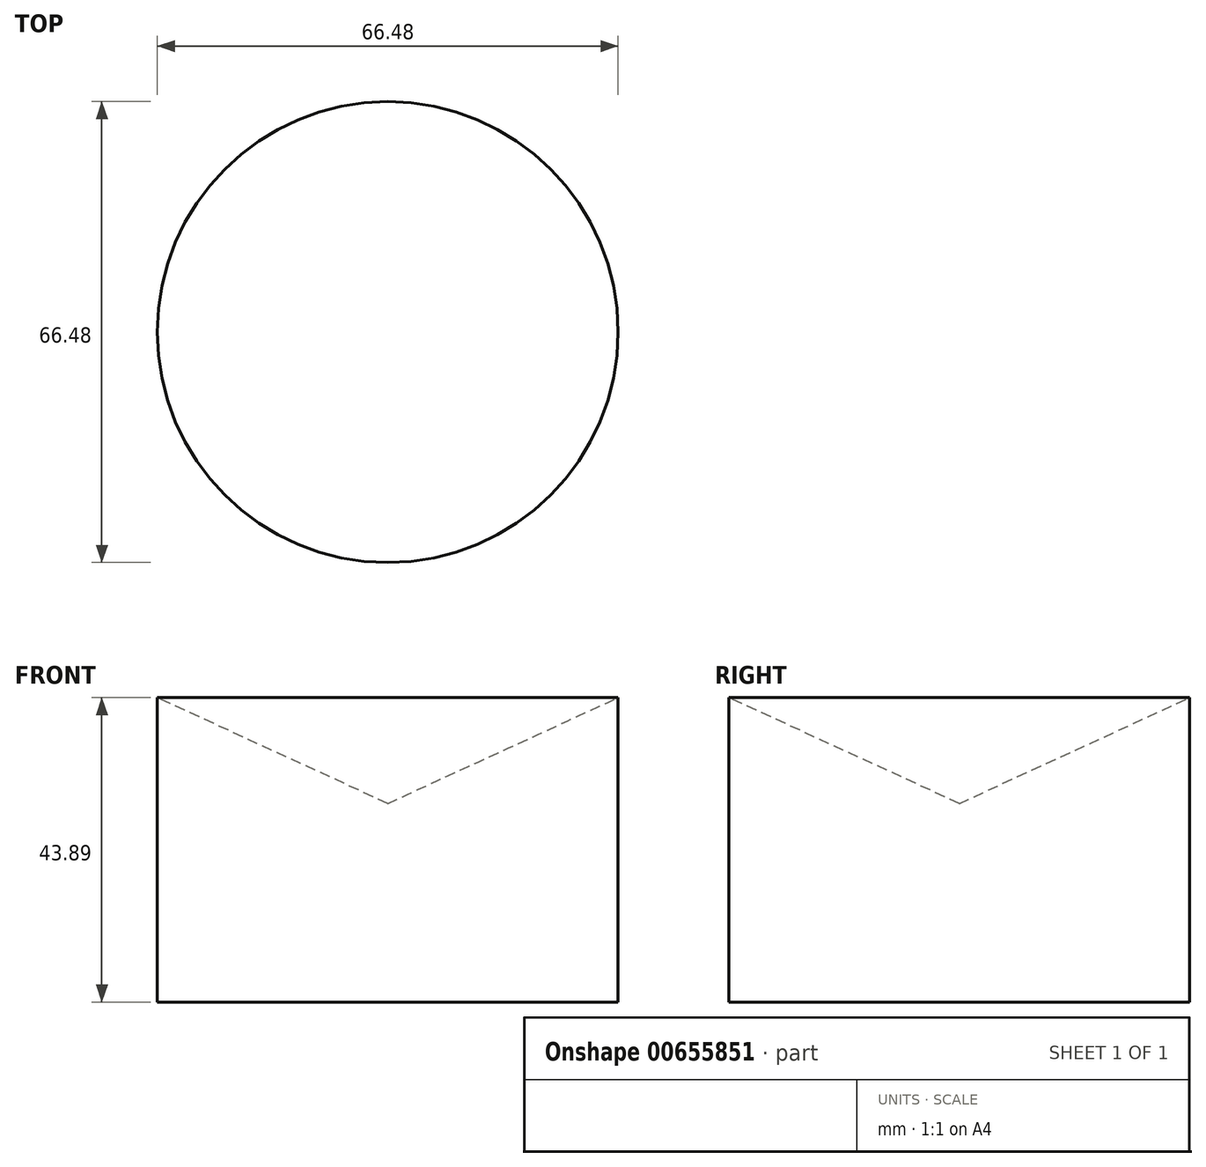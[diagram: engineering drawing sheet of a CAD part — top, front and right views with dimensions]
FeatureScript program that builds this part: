
annotation { "Feature Type Name" : "Feature", "Feature Type Description" : "" }
export const myFeature = defineFeature(function(context is Context, id is Id, definition is map)
    precondition{}
    {
        {
            var Q0;
            Q0=qCreatedBy(makeId("Front.planeOp"),FACE);
            var sketch = newSketch(context, id + "F0", { "sketchPlane" : qUnion([Q0])});
            skLineSegment(sketch, "E0", {"start": v(0, 28.64) * mm, "end": v(0, 0) * mm});
            skLineSegment(sketch, "E1", {"start": v(0, 0) * mm, "end": v(33.24, 0) * mm});
            skLineSegment(sketch, "E2", {"start": v(33.24, 0) * mm, "end": v(33.24, 43.9) * mm});
            skLineSegment(sketch, "E3", {"start": v(33.24, 43.9) * mm, "end": v(0, 28.64) * mm});
            skSolve(sketch);
        }
        {
            var Q0;
            Q0=makeQuery(id+"F0.imprint","IMPRINT",FACE,{"disambiguationData":[TD([[makeQuery(id+"F0.imprint","IMPRINT",EDGE,{"derivedFrom":sQuery(id+"F0.wireOp",EDGE,"E0")}),1.0]])]});
            var Q1;
            Q1=sQuery(id+"F0.wireOp",EDGE,"E0");
            revolve(context, id + "F1", {"entities" : qUnion([Q0]), "axis" : qUnion([Q1]), "revolveType" : RevolveType.FULL});
        }
    });
